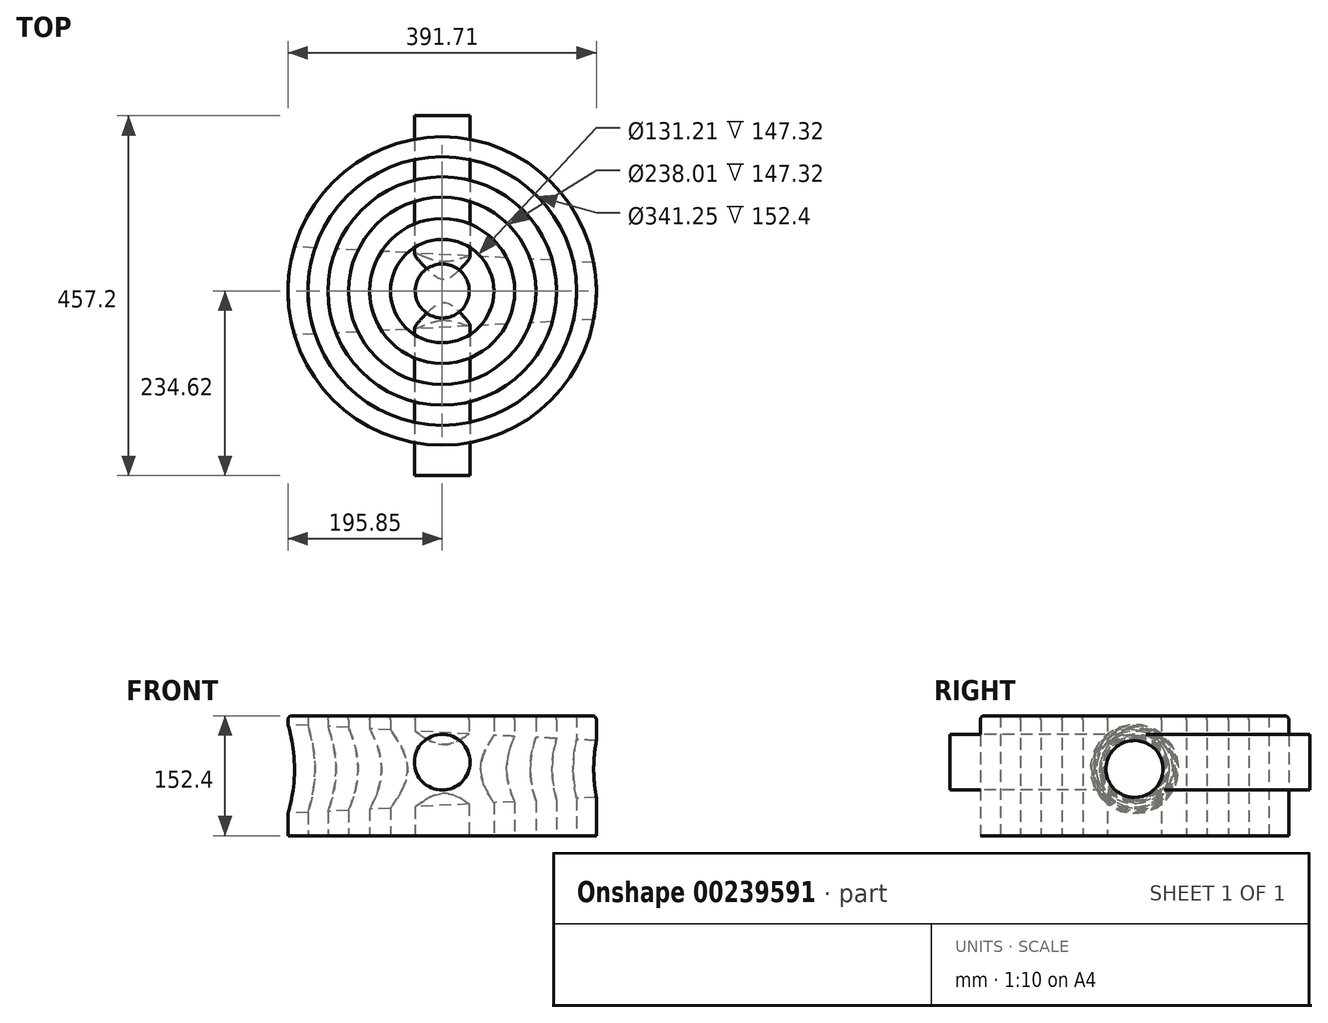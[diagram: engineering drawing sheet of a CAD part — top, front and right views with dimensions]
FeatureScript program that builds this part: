
annotation { "Feature Type Name" : "Feature", "Feature Type Description" : "" }
export const myFeature = defineFeature(function(context is Context, id is Id, definition is map)
    precondition{}
    {
        {
            var Q0;
            Q0=qCreatedBy(makeId("Top.planeOp"),FACE);
            var sketch = newSketch(context, id + "F0", { "sketchPlane" : qUnion([Q0])});
            skCircle(sketch, "E0", {"center": v(0, 0) * mm, "radius": 34.3 * mm});
            skCircle(sketch, "E1", {"center": v(0, 0) * mm, "radius": 65.6 * mm});
            skCircle(sketch, "E2", {"center": v(0, 0) * mm, "radius": 92.14 * mm});
            skCircle(sketch, "E3", {"center": v(0, 0) * mm, "radius": 119 * mm});
            skCircle(sketch, "E4", {"center": v(0, 0) * mm, "radius": 145.12 * mm});
            skCircle(sketch, "E5", {"center": v(0, 0) * mm, "radius": 170.63 * mm});
            skCircle(sketch, "E6", {"center": v(0, 0) * mm, "radius": 195.85 * mm});
            skSolve(sketch);
        }
        {
            var Q0;
            Q0 = qSketchRegion(id + "F0", true);
            var Q1;
            Q1=makeQuery(id+"F0.imprint","IMPRINT",FACE,{"disambiguationData":[TD([[makeQuery(id+"F0.imprint","IMPRINT",EDGE,{"derivedFrom":sQuery(id+"F0.wireOp",EDGE,"E0")}),1.0]])]});
            var Q2;
            Q2=makeQuery(id+"F0.imprint","IMPRINT",FACE,{"disambiguationData":[TD([[makeQuery(id+"F0.imprint","IMPRINT",EDGE,{"derivedFrom":sQuery(id+"F0.wireOp",EDGE,"E1")}),-1.0]])]});
            var Q3;
            Q3=makeQuery(id+"F0.imprint","IMPRINT",FACE,{"disambiguationData":[TD([[makeQuery(id+"F0.imprint","IMPRINT",EDGE,{"derivedFrom":sQuery(id+"F0.wireOp",EDGE,"E3")}),-1.0]])]});
            extrude(context, id + "F1", {"entities" : qUnion([Q0, Q1, Q2, Q3]), "depth" : 152.4 * mm});
        }
        {
            var Q0;
            Q0=makeQuery(id+"F1.opExtrude","CAP_EDGE",EDGE,{"disambiguationData":[OSD([sQuery(id+"F0.wireOp",EDGE,"E6")])],"isStart":false});
            var Q1;
            Q1=makeQuery(id+"F1.opExtrude","CAP_EDGE",EDGE,{"disambiguationData":[OSD([sQuery(id+"F0.wireOp",EDGE,"E4")])],"isStart":false});
            var Q2;
            Q2=makeQuery(id+"F1.opExtrude","CAP_EDGE",EDGE,{"disambiguationData":[OSD([sQuery(id+"F0.wireOp",EDGE,"E3")])],"isStart":false});
            var Q3;
            Q3=makeQuery(id+"F1.opExtrude","CAP_EDGE",EDGE,{"disambiguationData":[OSD([sQuery(id+"F0.wireOp",EDGE,"E2")])],"isStart":false});
            var Q4;
            Q4=makeQuery(id+"F1.opExtrude","CAP_EDGE",EDGE,{"disambiguationData":[OSD([sQuery(id+"F0.wireOp",EDGE,"E1")])],"isStart":false});
            var Q5;
            Q5=makeQuery(id+"F1.opExtrude","CAP_EDGE",EDGE,{"disambiguationData":[OSD([sQuery(id+"F0.wireOp",EDGE,"E0")])],"isStart":false});
            fillet(context, id + "F2", {"entities" : qUnion([Q0, Q1, Q2, Q3, Q4, Q5]), "radius" : 5.08 * mm, "tangentPropagation" : true, "allowEdgeOverflow" : false});
        }
        {
            var Q0;
            Q0=qCreatedBy(makeId("Front.planeOp"),FACE);
            cPlane(context, id + "F3", {"entities" : qUnion([Q0]), "cplaneType" : CPlaneType.OFFSET, "offset" : 234.62 * mm, "width" : 152.4 * mm, "height" : 152.4 * mm});
        }
        {
            var Q0;
            Q0=qCreatedBy(id+"F3.planeOp",FACE);
            var sketch = newSketch(context, id + "F4", { "sketchPlane" : qUnion([Q0])});
            skCircle(sketch, "E7", {"center": v(0, 93.42) * mm, "radius": 35.34 * mm});
            skSolve(sketch);
        }
        {
            var Q0;
            Q0 = qSketchRegion(id + "F4", true);
            extrude(context, id + "F5", {"entities" : qUnion([Q0]), "oppositeDirection" : true, "depth" : 457.2 * mm});
        }
        {
            var Q0;
            Q0=qCreatedBy(makeId("Right.planeOp"),FACE);
            cPlane(context, id + "F6", {"entities" : qUnion([Q0]), "cplaneType" : CPlaneType.OFFSET, "offset" : 203.2 * mm, "width" : 152.4 * mm, "height" : 152.4 * mm});
        }
        {
            var Q0;
            Q0=qCreatedBy(id+"F6.planeOp",FACE);
            var sketch = newSketch(context, id + "F7", { "sketchPlane" : qUnion([Q0])});
            skCircle(sketch, "E8", {"center": v(0, 84.76) * mm, "radius": 35.69 * mm});
            skSolve(sketch);
        }
        {
            var Q0;
            Q0 = qSketchRegion(id + "F7", true);
            extrude(context, id + "F8", {"entities" : qUnion([Q0]), "operationType" : NewBodyOperationType.REMOVE, "endBound" : BoundingType.THROUGH_ALL, "oppositeDirection" : true, "depth" : 438.93 * mm, "hasDraft" : true, "draftAngle" : 3 * degree, "hasSecondDirection" : true, "secondDirectionOppositeDirection" : false, "secondDirectionDepth" : 159.7 * mm});
        }
        {
            var Q0;
            Q0=qCreatedBy(makeId("Top.planeOp"),FACE);
            var sketch = newSketch(context, id + "F9", { "sketchPlane" : qUnion([Q0])});
            skLineSegment(sketch, "E9", {"start": v(0, -575.63) * mm, "end": v(0, -880.43) * mm});
            skLineSegment(sketch, "E10", {"start": v(-102.77, -273.6) * mm, "end": v(-102.77, -883.2) * mm});
            skLineSegment(sketch, "E11", {"start": v(-175.22, -0.82) * mm, "end": v(-175.22, -915.22) * mm});
            skLineSegment(sketch, "E12", {"start": v(-304.85, 245.04) * mm, "end": v(-304.85, -974.16) * mm});
            skLineSegment(sketch, "E13", {"start": v(-400.99, 511.42) * mm, "end": v(-400.99, -1012.58) * mm});
            skLineSegment(sketch, "E14", {"start": v(-564.74, 625.13) * mm, "end": v(-564.74, -1203.67) * mm});
            skLineSegment(sketch, "E15", {"start": v(-654.16, 863.1) * mm, "end": v(-654.16, -1270.5) * mm});
            skLineSegment(sketch, "E16", {"start": v(-809.13, 1164.61) * mm, "end": v(-809.13, -1273.79) * mm});
            skLineSegment(sketch, "E17", {"start": v(-944.84, 1380.6) * mm, "end": v(-944.84, -1362.6) * mm});
            skLineSegment(sketch, "E18", {"start": v(-1083.86, 1580.57) * mm, "end": v(-1083.86, -1467.43) * mm});
            skLineSegment(sketch, "E19", {"start": v(-1224.86, 1649.34) * mm, "end": v(-1224.86, -1703.46) * mm});
            skLineSegment(sketch, "E20", {"start": v(-1378.37, 1744.41) * mm, "end": v(-1378.37, -1913.19) * mm});
            skSolve(sketch);
        }
        {
            var Q0;
            Q0 = qSketchRegion(id + "F9", true);
            var Q1;
            Q1=sQuery(id+"F9.wireOp",EDGE,"E20");
            var Q2;
            Q2=sQuery(id+"F9.wireOp",EDGE,"E19");
            var Q3;
            Q3=sQuery(id+"F9.wireOp",EDGE,"E18");
            var Q4;
            Q4=sQuery(id+"F9.wireOp",EDGE,"E17");
            var Q5;
            Q5=sQuery(id+"F9.wireOp",EDGE,"E16");
            var Q6;
            Q6=sQuery(id+"F9.wireOp",EDGE,"E14");
            var Q7;
            Q7=sQuery(id+"F9.wireOp",EDGE,"E13");
            var Q8;
            Q8=sQuery(id+"F9.wireOp",EDGE,"E15");
            var Q9;
            Q9=sQuery(id+"F9.wireOp",EDGE,"E11");
            var Q10;
            Q10=sQuery(id+"F9.wireOp",EDGE,"E12");
            var Q11;
            Q11=sQuery(id+"F9.wireOp",EDGE,"E10");
            var Q12;
            Q12=sQuery(id+"F9.wireOp",EDGE,"E9");
            extrude(context, id + "F10", {"entities" : qUnion([Q0]), "bodyType" : ToolBodyType.SURFACE, "surfaceEntities" : qUnion([Q1, Q2, Q3, Q4, Q5, Q6, Q7, Q8, Q9, Q10, Q11, Q12]), "depth" : 457.2 * mm});
        }
    });
